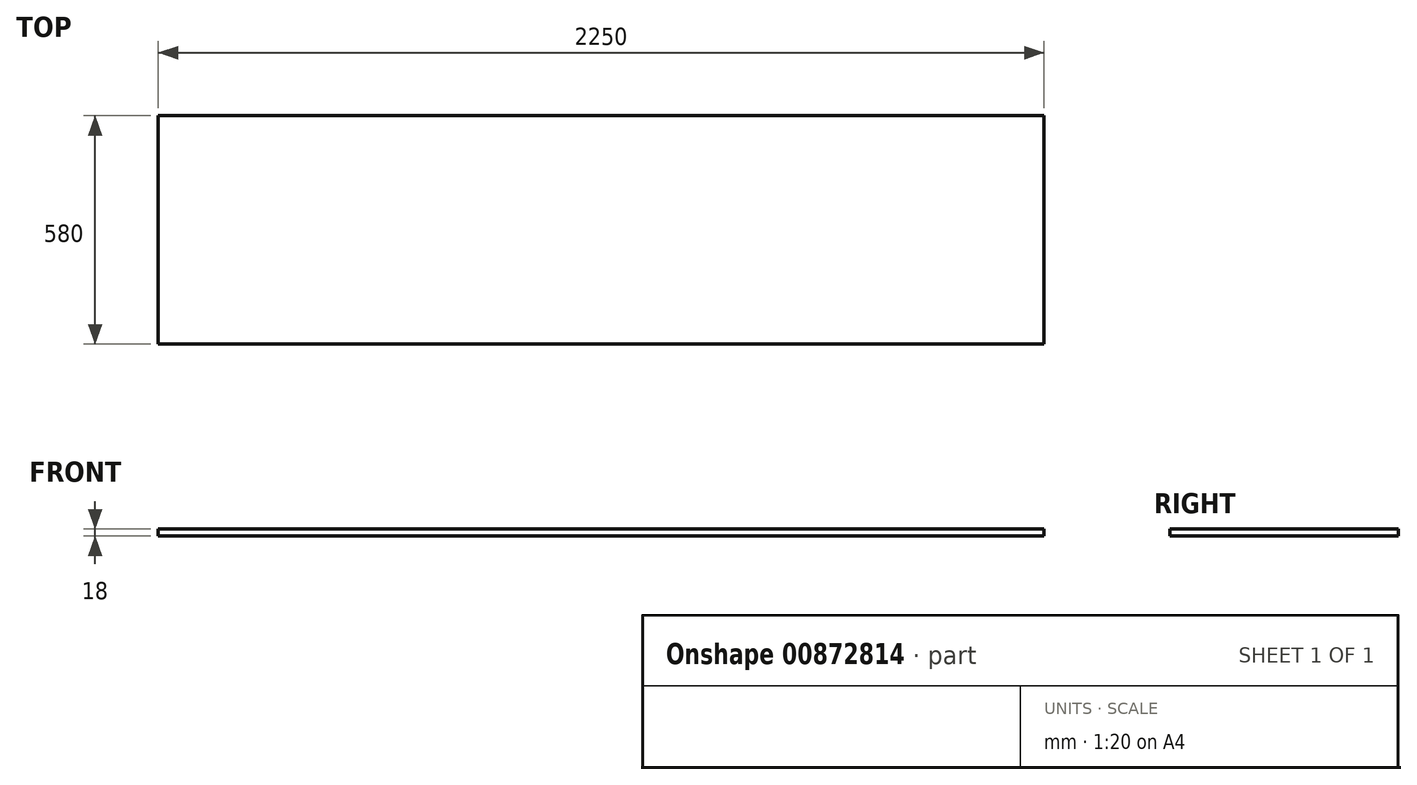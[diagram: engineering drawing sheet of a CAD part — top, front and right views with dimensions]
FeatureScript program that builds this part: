
annotation { "Feature Type Name" : "Feature", "Feature Type Description" : "" }
export const myFeature = defineFeature(function(context is Context, id is Id, definition is map)
    precondition{}
    {
        {
            var Q0;
            Q0=qCreatedBy(makeId("Top.planeOp"),FACE);
            var sketch = newSketch(context, id + "F0", { "sketchPlane" : qUnion([Q0])});
            skLineSegment(sketch, "E0.bottom", {"start": v(1125, 290) * mm, "end": v(-1125, 290) * mm});
            skLineSegment(sketch, "E0.top", {"start": v(1125, -290) * mm, "end": v(-1125, -290) * mm});
            skLineSegment(sketch, "E0.left", {"start": v(1125, 290) * mm, "end": v(1125, -290) * mm});
            skLineSegment(sketch, "E0.right", {"start": v(-1125, 290) * mm, "end": v(-1125, -290) * mm});
            skPoint(sketch, "E0.middle", {"position": v(0, 0) * mm});
            skSolve(sketch);
        }
        {
            var Q0;
            Q0 = qSketchRegion(id + "F0", true);
            extrude(context, id + "F1", {"entities" : qUnion([Q0]), "depth" : 18 * mm, "offsetDistance" : 25 * mm});
        }
    });
